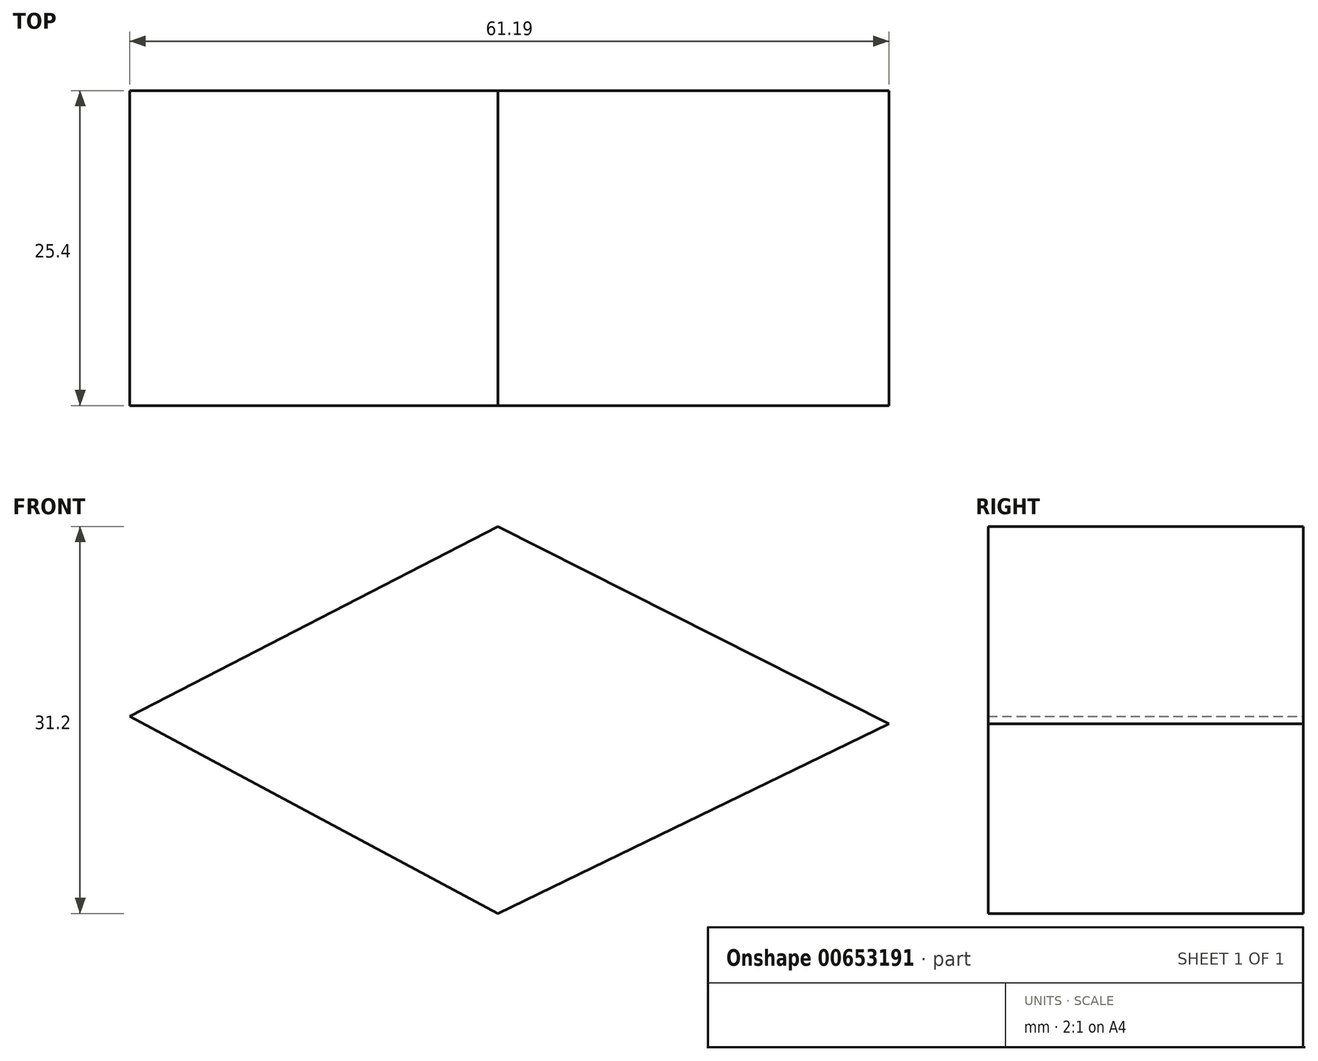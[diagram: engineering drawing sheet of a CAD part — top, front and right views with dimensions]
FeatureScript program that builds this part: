
annotation { "Feature Type Name" : "Feature", "Feature Type Description" : "" }
export const myFeature = defineFeature(function(context is Context, id is Id, definition is map)
    precondition{}
    {
        {
            var Q0;
            Q0=qCreatedBy(makeId("Front.planeOp"),FACE);
            var sketch = newSketch(context, id + "F0", { "sketchPlane" : qUnion([Q0])});
            skLineSegment(sketch, "E0", {"start": v(23.87, 37.63) * mm, "end": v(55.38, 21.72) * mm});
            skLineSegment(sketch, "E1", {"start": v(55.38, 21.72) * mm, "end": v(23.87, 6.43) * mm});
            skLineSegment(sketch, "E2", {"start": v(23.87, 6.43) * mm, "end": v(-5.81, 22.34) * mm});
            skLineSegment(sketch, "E3", {"start": v(-5.81, 22.34) * mm, "end": v(23.87, 37.63) * mm});
            skSolve(sketch);
        }
        {
            var Q0;
            Q0 = qSketchRegion(id + "F0", true);
            extrude(context, id + "F1", {"entities" : qUnion([Q0]), "depth" : 25.4 * mm, "offsetDistance" : 25.4 * mm});
        }
    });
